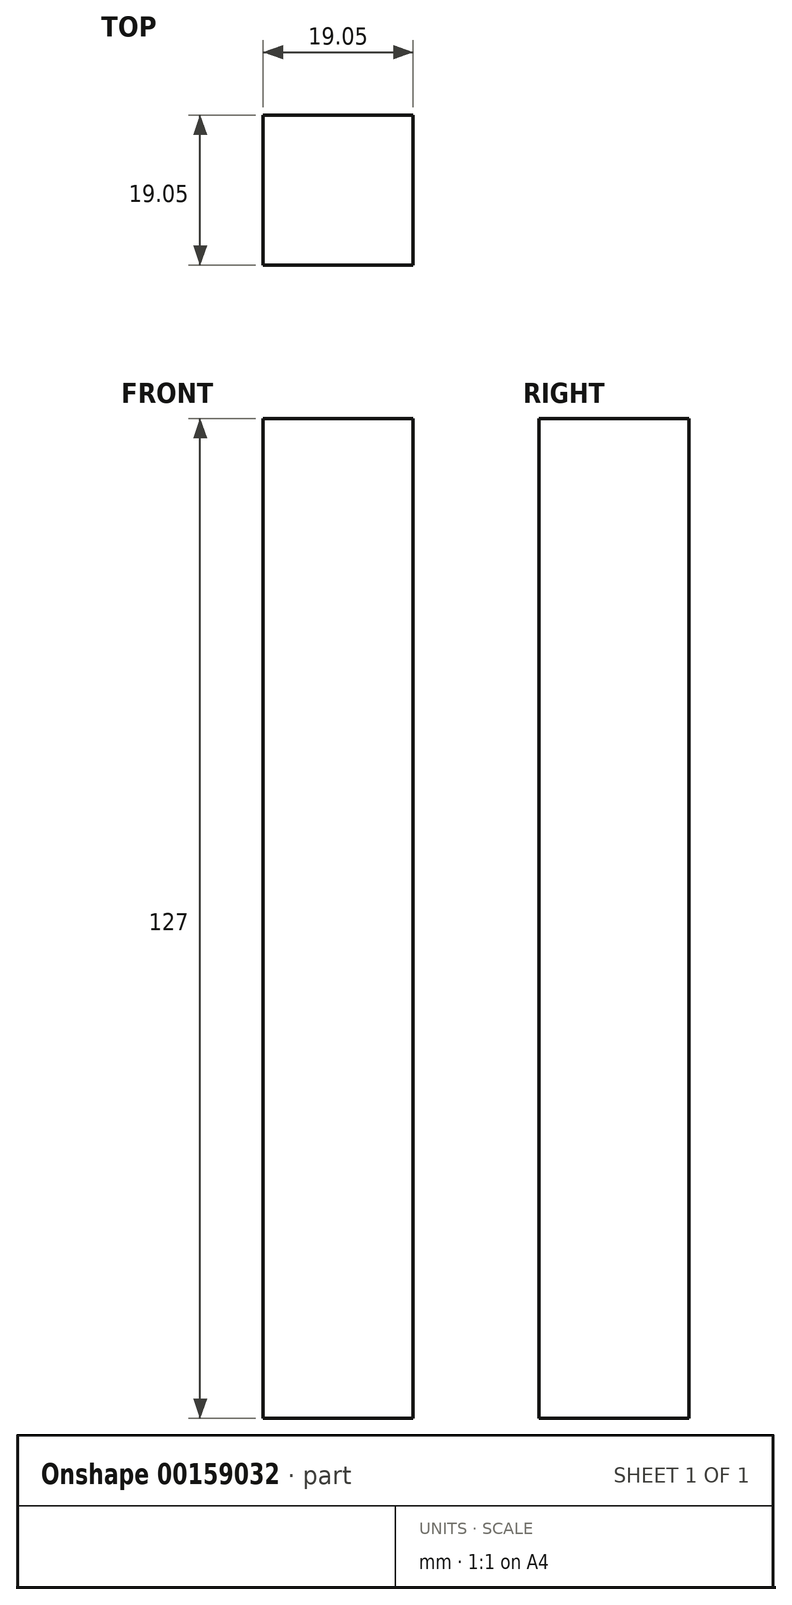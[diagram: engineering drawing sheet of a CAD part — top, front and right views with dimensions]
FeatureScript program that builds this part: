
annotation { "Feature Type Name" : "Feature", "Feature Type Description" : "" }
export const myFeature = defineFeature(function(context is Context, id is Id, definition is map)
    precondition{}
    {
        {
            var Q0;
            Q0=qCreatedBy(makeId("Top.planeOp"),FACE);
            var sketch = newSketch(context, id + "F0", { "sketchPlane" : qUnion([Q0])});
            skLineSegment(sketch, "E0.bottom", {"start": v(-21.21, -15.02) * mm, "end": v(-2.16, -15.02) * mm});
            skLineSegment(sketch, "E0.top", {"start": v(-21.21, 4.03) * mm, "end": v(-2.16, 4.03) * mm});
            skLineSegment(sketch, "E0.left", {"start": v(-21.21, -15.02) * mm, "end": v(-21.21, 4.03) * mm});
            skLineSegment(sketch, "E0.right", {"start": v(-2.16, -15.02) * mm, "end": v(-2.16, 4.03) * mm});
            skSolve(sketch);
        }
        {
            var Q0;
            Q0 = qSketchRegion(id + "F0", true);
            extrude(context, id + "F1", {"entities" : qUnion([Q0]), "depth" : 127 * mm});
        }
    });
